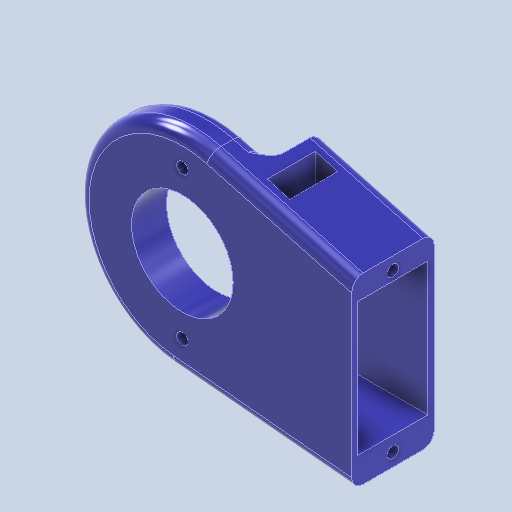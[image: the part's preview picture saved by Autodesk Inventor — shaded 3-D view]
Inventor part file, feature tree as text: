
AUTODESK INVENTOR PART (.ipt)
format: ipt  version: 2023.2 (Build 272271000, 271)  size: 379,904 bytes
history: native  units: mm
features: sketch x6, extrude x4, hole x2, fillet x1
ambient origin geometry x8: Origin, YZ Plane, XZ Plane, XY Plane, X Axis, Y Axis, Z Axis, Center Point
bodies: Solid1 (feature_tree)
feature tree (13):
  extrude  "Extrusion1"  Depth=32.4mm
  extrude  "Extrusion3"  Depth=12.4mm
  extrude  "Extrusion4"  Depth=8.5mm
  extrude  "Extrusion5"  TaperAngle=0.0deg  [1 undecoded]
  hole  "Hole2"  [1 undecoded]
  fillet  "Fillet1"  Radius=10.0mm
  hole  "Hole3"  [1 undecoded]
  sketch  "Sketch1"  dims[d2=14.6mm d3=0.0mm d13=32.4mm]
  sketch  "Sketch4"  dims[d22=8.4mm d23=0.0mm d25=12.4mm]
  sketch  "Sketch5"  dims[d26=18.0mm d27=0.0mm d28=8.5mm]
  sketch  "Sketch6"  dims[d29=4.0mm d30=0.0mm d31=0.0mm]
  sketch  "Sketch7"  dims[d32=27.8mm]
  sketch  "Sketch8"  dims[d33=2.0mm d34=6.0mm d35=4.0mm d36=2.0mm d37=90.0deg d38=7.0mm d39=0.0mm d40=37.0mm d41=10.0mm d42=30.0mm d43=2.0mm d45=5.2mm d46=18.0mm d47=26.2mm d48=2.0mm d49=6.0mm d50=4.0mm d51=2.0mm d52=90.0deg d53=8.0mm d54=0.0mm d55=27.8mm d56=22.6mm d57=23.6mm]
note: 3 required parameter values undecoded (feature->parameter linkage not recoverable at this tier; creation-order binding heuristic only, values carry confidence <= 0.55)
